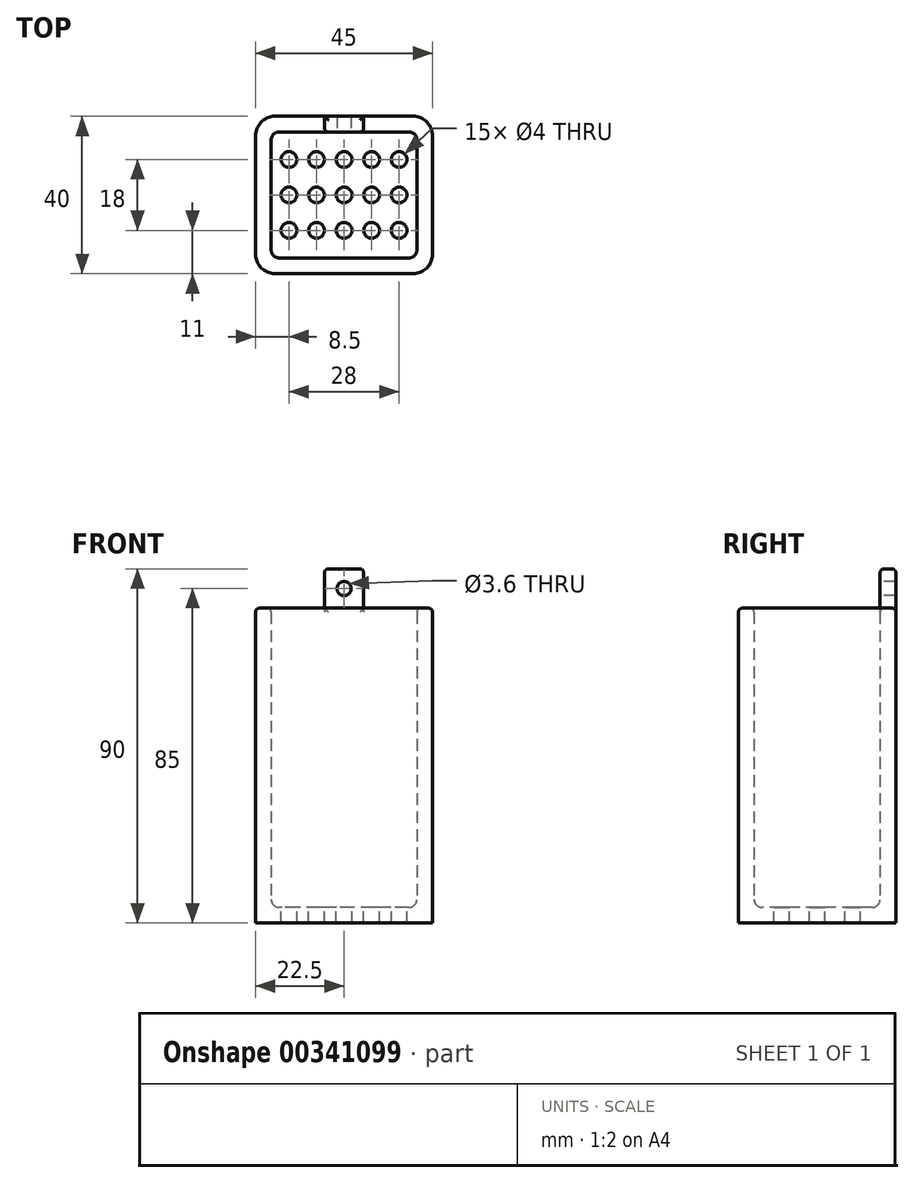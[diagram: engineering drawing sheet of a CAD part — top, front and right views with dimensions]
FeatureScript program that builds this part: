
annotation { "Feature Type Name" : "Feature", "Feature Type Description" : "" }
export const myFeature = defineFeature(function(context is Context, id is Id, definition is map)
    precondition{}
    {
        {
            var Q0;
            Q0=qCreatedBy(makeId("Top.planeOp"),FACE);
            var sketch = newSketch(context, id + "F0", { "sketchPlane" : qUnion([Q0])});
            skLineSegment(sketch, "E0.bottom", {"start": v(22.5, 20) * mm, "end": v(-22.5, 20) * mm});
            skLineSegment(sketch, "E0.top", {"start": v(22.5, -20) * mm, "end": v(-22.5, -20) * mm});
            skLineSegment(sketch, "E0.left", {"start": v(22.5, 20) * mm, "end": v(22.5, -20) * mm});
            skLineSegment(sketch, "E0.right", {"start": v(-22.5, 20) * mm, "end": v(-22.5, -20) * mm});
            skPoint(sketch, "E0.middle", {"position": v(0, 0) * mm});
            skSolve(sketch);
        }
        {
            var Q0;
            Q0 = qSketchRegion(id + "F0", true);
            extrude(context, id + "F1", {"entities" : qUnion([Q0]), "depth" : 80 * mm});
        }
        {
            var Q0;
            Q0=makeQuery(id+"F1.opExtrude","CAP_FACE",FACE,{"disambiguationData":[OSD([sQuery(id+"F0.wireOp",EDGE,"E0.bottom"),sQuery(id+"F0.wireOp",EDGE,"E0.top"),sQuery(id+"F0.wireOp",EDGE,"E0.left"),sQuery(id+"F0.wireOp",EDGE,"E0.right")])],"isStart":false});
            shell(context, id + "F2", {"entities" : qUnion([Q0]), "thickness" : 4 * mm});
        }
        {
            var Q0;
            Q0=makeQuery(id+"F2.opShell","OFFSET_FACE",FACE,{"disambiguationData":[OSD([sQuery(id+"F0.wireOp",EDGE,"E0.bottom"),sQuery(id+"F0.wireOp",EDGE,"E0.top"),sQuery(id+"F0.wireOp",EDGE,"E0.left"),sQuery(id+"F0.wireOp",EDGE,"E0.right")])]});
            var Q1;
            Q1=makeQuery(id+"F2.opShell","OFFSET_EDGE",EDGE,{"disambiguationData":[OSD([sQuery(id+"F0.wireOp",EDGE,"E0.bottom"),sQuery(id+"F0.wireOp",EDGE,"E0.right")])]});
            var Q2;
            Q2=makeQuery(id+"F2.opShell","OFFSET_EDGE",EDGE,{"disambiguationData":[OSD([sQuery(id+"F0.wireOp",EDGE,"E0.bottom"),sQuery(id+"F0.wireOp",EDGE,"E0.left")])]});
            var Q3;
            Q3=makeQuery(id+"F2.opShell","OFFSET_EDGE",EDGE,{"disambiguationData":[OSD([sQuery(id+"F0.wireOp",EDGE,"E0.top"),sQuery(id+"F0.wireOp",EDGE,"E0.left")])]});
            var Q4;
            Q4=makeQuery(id+"F2.opShell","OFFSET_EDGE",EDGE,{"disambiguationData":[OSD([sQuery(id+"F0.wireOp",EDGE,"E0.top"),sQuery(id+"F0.wireOp",EDGE,"E0.right")])]});
            fillet(context, id + "F3", {"entities" : qUnion([Q0, Q1, Q2, Q3, Q4]), "radius" : 2 * mm, "tangentPropagation" : true, "allowEdgeOverflow" : false});
        }
        {
            var Q0;
            Q0=makeQuery(id+"F1.opExtrude","SWEPT_EDGE",EDGE,{"disambiguationData":[OSD([sQuery(id+"F0.wireOp",EDGE,"E0.top"),sQuery(id+"F0.wireOp",EDGE,"E0.right")])]});
            var Q1;
            Q1=makeQuery(id+"F1.opExtrude","SWEPT_EDGE",EDGE,{"disambiguationData":[OSD([sQuery(id+"F0.wireOp",EDGE,"E0.bottom"),sQuery(id+"F0.wireOp",EDGE,"E0.right")])]});
            var Q2;
            Q2=makeQuery(id+"F1.opExtrude","SWEPT_EDGE",EDGE,{"disambiguationData":[OSD([sQuery(id+"F0.wireOp",EDGE,"E0.top"),sQuery(id+"F0.wireOp",EDGE,"E0.left")])]});
            var Q3;
            Q3=makeQuery(id+"F1.opExtrude","SWEPT_EDGE",EDGE,{"disambiguationData":[OSD([sQuery(id+"F0.wireOp",EDGE,"E0.bottom"),sQuery(id+"F0.wireOp",EDGE,"E0.left")])]});
            fillet(context, id + "F4", {"entities" : qUnion([Q0, Q1, Q2, Q3]), "radius" : 5 * mm, "tangentPropagation" : true, "allowEdgeOverflow" : false});
        }
        {
            var Q0;
            Q0=makeQuery(id+"F2.opShell","OFFSET_FACE",FACE,{"disambiguationData":[OSD([sQuery(id+"F0.wireOp",EDGE,"E0.bottom"),sQuery(id+"F0.wireOp",EDGE,"E0.top"),sQuery(id+"F0.wireOp",EDGE,"E0.left"),sQuery(id+"F0.wireOp",EDGE,"E0.right")])]});
            var sketch = newSketch(context, id + "F5", { "sketchPlane" : qUnion([Q0])});
            skCircle(sketch, "E1", {"center": v(0, 0) * mm, "radius": 2 * mm});
            skCircle(sketch, "E2.0.1.0", {"center": v(0, 9) * mm, "radius": 2 * mm});
            skCircle(sketch, "E2.1.0.0", {"center": v(7, 0) * mm, "radius": 2 * mm});
            skCircle(sketch, "E2.1.1.0", {"center": v(7, 9) * mm, "radius": 2 * mm});
            skCircle(sketch, "E2.2.0.0", {"center": v(14, 0) * mm, "radius": 2 * mm});
            skCircle(sketch, "E2.2.1.0", {"center": v(14, 9) * mm, "radius": 2 * mm});
            skLineSegment(sketch, "E2.direction1", {"start": v(0, 0) * mm, "end": v(7, 0) * mm, "construction": true});
            skLineSegment(sketch, "E2.direction2", {"start": v(0, 0) * mm, "end": v(0, 9) * mm, "construction": true});
            skCircle(sketch, "E3.MirrorC", {"center": v(-7, 9) * mm, "radius": 2 * mm});
            skCircle(sketch, "E4.MirrorC", {"center": v(-14, 9) * mm, "radius": 2 * mm});
            skCircle(sketch, "E5.MirrorC", {"center": v(-7, 0) * mm, "radius": 2 * mm});
            skCircle(sketch, "E6.MirrorC", {"center": v(-14, 0) * mm, "radius": 2 * mm});
            skCircle(sketch, "E7.MirrorC", {"center": v(-14, -9) * mm, "radius": 2 * mm});
            skCircle(sketch, "E8.MirrorC", {"center": v(-7, -9) * mm, "radius": 2 * mm});
            skCircle(sketch, "E9.MirrorC", {"center": v(7, -9) * mm, "radius": 2 * mm});
            skCircle(sketch, "E10.MirrorC", {"center": v(0, -9) * mm, "radius": 2 * mm});
            skCircle(sketch, "E11.MirrorC", {"center": v(14, -9) * mm, "radius": 2 * mm});
            skSolve(sketch);
        }
        {
            var Q0;
            Q0 = qSketchRegion(id + "F5", true);
            extrude(context, id + "F6", {"entities" : qUnion([Q0]), "operationType" : NewBodyOperationType.REMOVE, "endBound" : BoundingType.THROUGH_ALL, "oppositeDirection" : true, "depth" : 25 * mm});
        }
        {
            var Q0;
            Q0=makeQuery(id+"F1.opExtrude","CAP_FACE",FACE,{"disambiguationData":[OSD([sQuery(id+"F0.wireOp",EDGE,"E0.bottom"),sQuery(id+"F0.wireOp",EDGE,"E0.top"),sQuery(id+"F0.wireOp",EDGE,"E0.left"),sQuery(id+"F0.wireOp",EDGE,"E0.right")])],"isStart":false});
            var sketch = newSketch(context, id + "F7", { "sketchPlane" : qUnion([Q0])});
            skLineSegment(sketch, "E12", {"start": v(0, 20) * mm, "end": v(5, 20) * mm});
            skLineSegment(sketch, "E13", {"start": v(5, 20) * mm, "end": v(5, 16) * mm});
            skLineSegment(sketch, "E14", {"start": v(5, 16) * mm, "end": v(-5, 16) * mm});
            skLineSegment(sketch, "E15", {"start": v(-5, 16) * mm, "end": v(-5, 20) * mm});
            skLineSegment(sketch, "E16", {"start": v(-5, 20) * mm, "end": v(0, 20) * mm});
            skSolve(sketch);
        }
        {
            var Q0;
            Q0 = qSketchRegion(id + "F7", true);
            extrude(context, id + "F8", {"entities" : qUnion([Q0]), "operationType" : NewBodyOperationType.ADD, "depth" : 10 * mm});
        }
        {
            var Q0;
            Q0=makeQuery(id+"F8.boolean.opBoolean","MERGE",FACE,{"derivedFrom":[makeQuery(id+"F2.opShell","OFFSET_FACE",FACE,{"disambiguationData":[OSD([sQuery(id+"F0.wireOp",EDGE,"E0.bottom")])]}),makeQuery(id+"F8.opExtrude","SWEPT_FACE",FACE,{"disambiguationData":[OSD([sQuery(id+"F7.wireOp",EDGE,"E14")])]})]});
            var sketch = newSketch(context, id + "F9", { "sketchPlane" : qUnion([Q0])});
            skLineSegment(sketch, "E17", {"start": v(0, 90) * mm, "end": v(0, 85) * mm, "construction": true});
            skPoint(sketch, "E17.endSnap0", {"position": v(0, 90) * mm});
            skCircle(sketch, "E18", {"center": v(0, 85) * mm, "radius": 1.8 * mm});
            skSolve(sketch);
        }
        {
            var Q0;
            Q0 = qSketchRegion(id + "F9", true);
            extrude(context, id + "F10", {"entities" : qUnion([Q0]), "operationType" : NewBodyOperationType.REMOVE, "oppositeDirection" : true, "depth" : 25 * mm});
        }
        {
            var Q0;
            Q0=makeQuery(id+"F1.opExtrude","CAP_EDGE",EDGE,{"disambiguationData":[OSD([sQuery(id+"F0.wireOp",EDGE,"E0.left")])],"isStart":false});
            var Q1;
            {var subQ0=sQuery(id+"F0.wireOp",EDGE,"E0.top");Q1=makeQuery(id+"F2.opShell","OFFSET_EDGE",EDGE,{"disambiguationData":[OSD([subQ0]),TDD([makeQuery(id+"F1.opExtrude","CAP_EDGE",EDGE,{"disambiguationData":[OSD([subQ0])],"isStart":false})])]});}
            fillet(context, id + "F11", {"entities" : qUnion([Q0, Q1]), "radius" : 1 * mm, "tangentPropagation" : true, "allowEdgeOverflow" : false});
        }
        {
            var Q0;
            Q0=makeQuery(id+"F8.opExtrude","CAP_EDGE",EDGE,{"disambiguationData":[OSD([sQuery(id+"F7.wireOp",EDGE,"E14")])],"isStart":false});
            var Q1;
            Q1=makeQuery(id+"F8.opExtrude","CAP_EDGE",EDGE,{"disambiguationData":[OSD([sQuery(id+"F7.wireOp",EDGE,"E12"),sQuery(id+"F7.wireOp",EDGE,"E16")])],"isStart":false});
            var Q2;
            Q2=makeQuery(id+"F8.opExtrude","CAP_EDGE",EDGE,{"disambiguationData":[OSD([sQuery(id+"F7.wireOp",EDGE,"E15")])],"isStart":false});
            var Q3;
            Q3=makeQuery(id+"F8.opExtrude","CAP_EDGE",EDGE,{"disambiguationData":[OSD([sQuery(id+"F7.wireOp",EDGE,"E13")])],"isStart":false});
            fillet(context, id + "F12", {"entities" : qUnion([Q0, Q1, Q2, Q3]), "radius" : 1 * mm, "tangentPropagation" : true, "allowEdgeOverflow" : false});
        }
        {
            var Q0;
            Q0=makeQuery(id+"F8.opExtrude","SWEPT_EDGE",EDGE,{"disambiguationData":[OSD([sQuery(id+"F0.wireOp",EDGE,"E0.bottom"),sQuery(id+"F7.wireOp",EDGE,"E13"),sQuery(id+"F7.wireOp",EDGE,"E14")])]});
            var Q1;
            Q1=makeQuery(id+"F8.opExtrude","SWEPT_EDGE",EDGE,{"disambiguationData":[OSD([sQuery(id+"F0.wireOp",EDGE,"E0.bottom"),sQuery(id+"F7.wireOp",EDGE,"E14"),sQuery(id+"F7.wireOp",EDGE,"E15")])]});
            fillet(context, id + "F13", {"entities" : qUnion([Q0, Q1]), "radius" : 1 * mm, "tangentPropagation" : true, "allowEdgeOverflow" : false});
        }
    });
